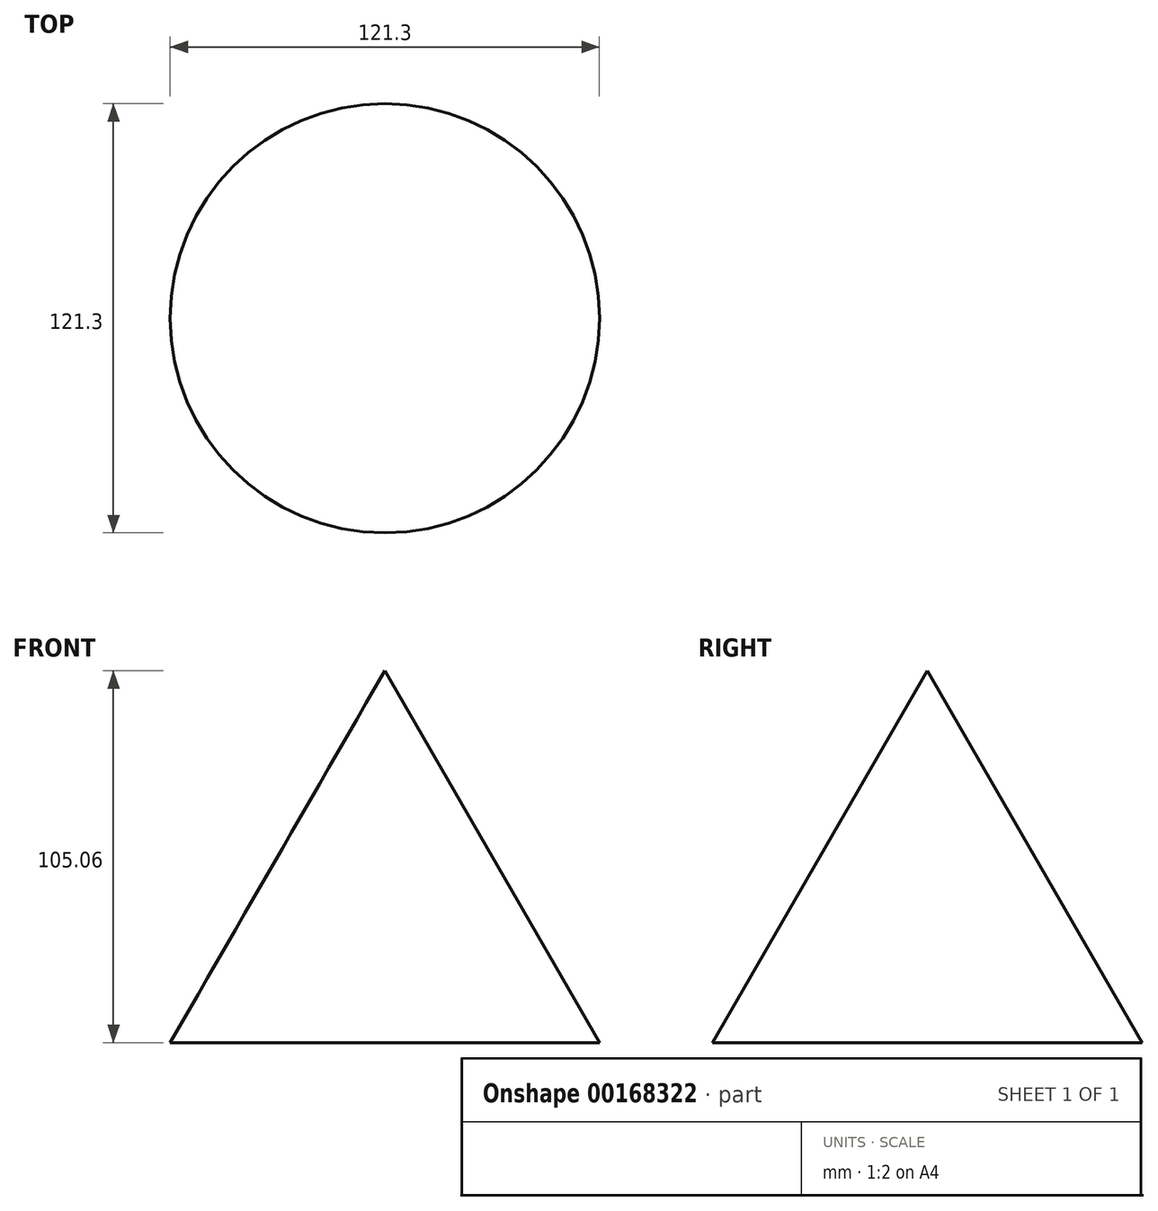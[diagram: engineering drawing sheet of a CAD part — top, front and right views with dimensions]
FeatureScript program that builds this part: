
annotation { "Feature Type Name" : "Feature", "Feature Type Description" : "" }
export const myFeature = defineFeature(function(context is Context, id is Id, definition is map)
    precondition{}
    {
        {
            var Q0;
            Q0=qCreatedBy(makeId("Front.planeOp"),FACE);
            var sketch = newSketch(context, id + "F0", { "sketchPlane" : qUnion([Q0])});
            skLineSegment(sketch, "E0.0", {"start": v(0, -35.02) * mm, "end": v(-60.65, -35.02) * mm});
            skLineSegment(sketch, "E0.1", {"start": v(-60.65, -35.02) * mm, "end": v(0, 70.04) * mm});
            skPoint(sketch, "E0.0.midPoint", {"position": v(0, -35.02) * mm});
            skPoint(sketch, "E0.cCircle.center.orphan", {"position": v(0, 0) * mm});
            skPoint(sketch, "E1.orphan", {"position": v(60.65, -35.02) * mm});
            skLineSegment(sketch, "E2", {"start": v(0, 70.04) * mm, "end": v(0, -35.02) * mm});
            skSolve(sketch);
        }
        {
            var Q0;
            Q0 = qSketchRegion(id + "F0", true);
            var Q1;
            Q1=sQuery(id+"F0.wireOp",EDGE,"E2");
            revolve(context, id + "F1", {"entities" : qUnion([Q0]), "axis" : qUnion([Q1]), "revolveType" : RevolveType.FULL});
        }
    });
